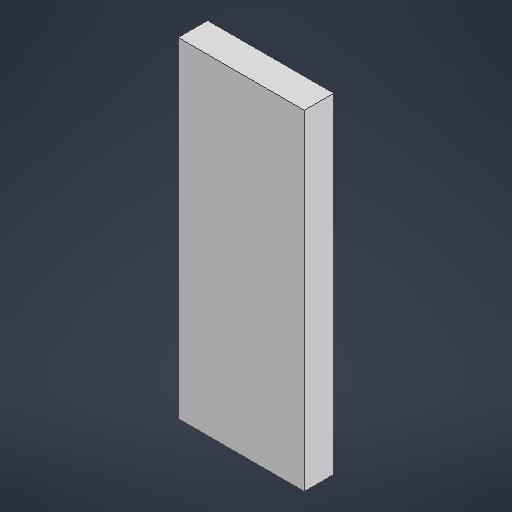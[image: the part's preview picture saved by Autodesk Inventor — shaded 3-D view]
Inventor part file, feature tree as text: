
AUTODESK INVENTOR PART (.ipt)
format: ipt  version: 2025 (Build 290162000, 162)  size: 188,928 bytes
history: native  units: mm
features: extrude x1, sketch x1
ambient origin geometry x8: Origin, YZ Plane, XZ Plane, XY Plane, X Axis, Y Axis, Z Axis, Center Point
bodies: 实体1 (feature_tree)
feature tree (2):
  extrude  "拉伸1"  Depth=21.4mm
  sketch  "草图1"  dims[d0=56.0mm d1=21.4mm d2=5.0mm d3=0.0mm]
